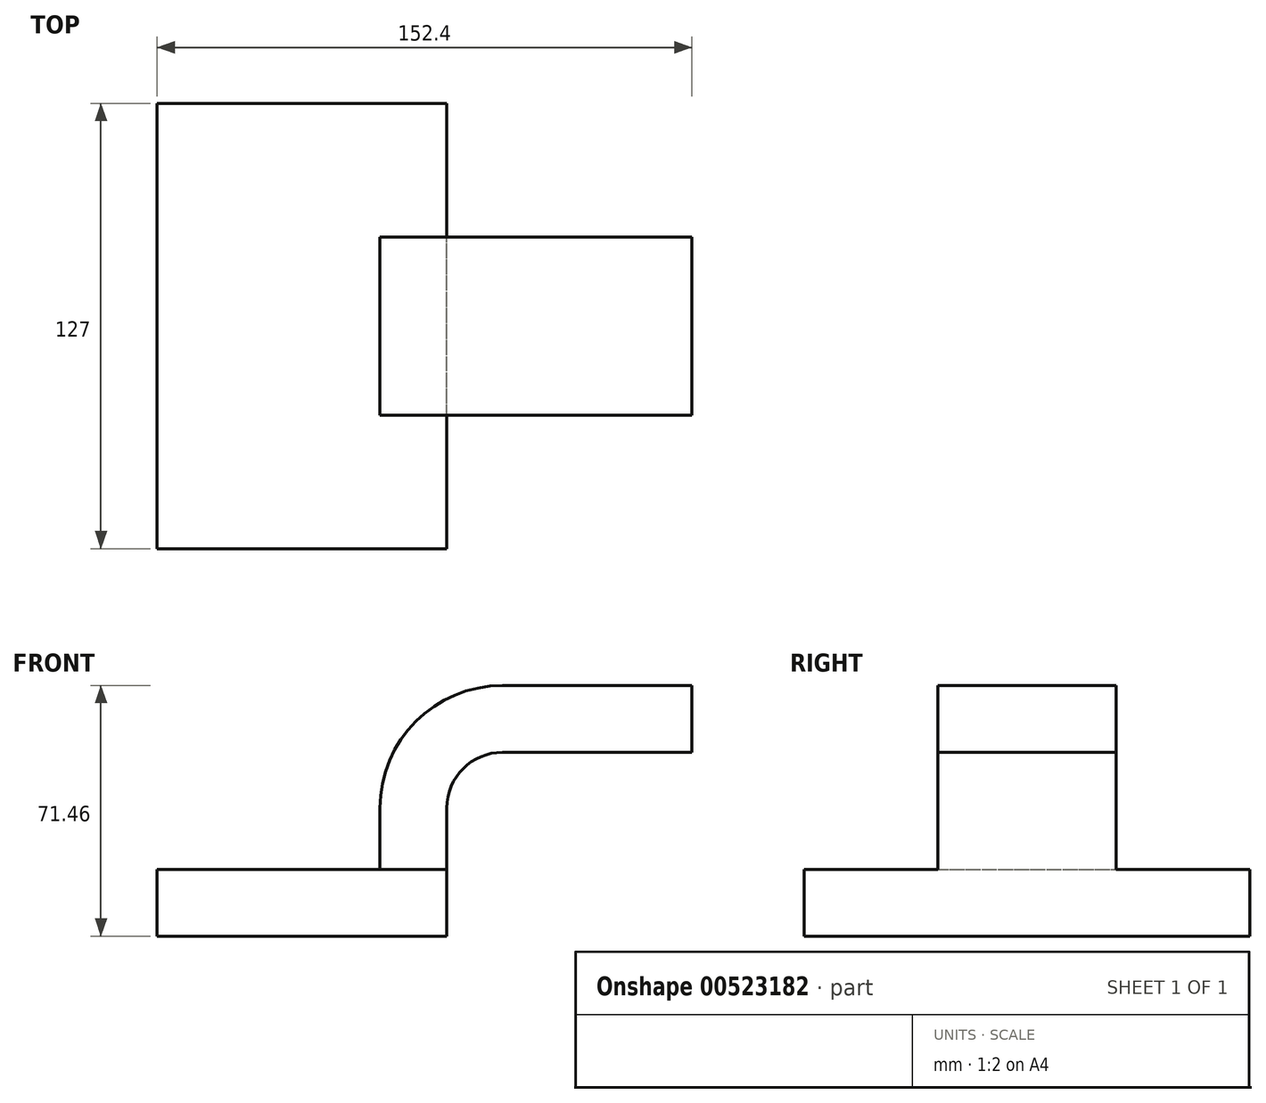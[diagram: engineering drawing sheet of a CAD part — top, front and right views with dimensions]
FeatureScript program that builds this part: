
annotation { "Feature Type Name" : "Feature", "Feature Type Description" : "" }
export const myFeature = defineFeature(function(context is Context, id is Id, definition is map)
    precondition{}
    {
        {
            var Q0;
            Q0=qCreatedBy(makeId("Front.planeOp"),FACE);
            var sketch = newSketch(context, id + "F0", { "sketchPlane" : qUnion([Q0])});
            skLineSegment(sketch, "E0.bottom", {"start": v(41.27, 9.53) * mm, "end": v(-41.28, 9.53) * mm});
            skLineSegment(sketch, "E0.top", {"start": v(41.28, -9.52) * mm, "end": v(-41.27, -9.52) * mm});
            skLineSegment(sketch, "E0.left", {"start": v(41.27, 9.53) * mm, "end": v(41.28, -9.52) * mm});
            skLineSegment(sketch, "E0.right", {"start": v(-41.28, 9.53) * mm, "end": v(-41.27, -9.52) * mm});
            skPoint(sketch, "E0.middle", {"position": v(0, 0) * mm});
            skLineSegment(sketch, "E1.bottom", {"start": v(60.32, 66.68) * mm, "end": v(111.12, 66.68) * mm});
            skLineSegment(sketch, "E1.top", {"start": v(60.32, 38.1) * mm, "end": v(111.12, 38.1) * mm});
            skLineSegment(sketch, "E1.left", {"start": v(60.32, 66.68) * mm, "end": v(60.32, 38.1) * mm});
            skLineSegment(sketch, "E1.right", {"start": v(111.12, 66.68) * mm, "end": v(111.12, 38.1) * mm});
            skPoint(sketch, "E1.middle", {"position": v(85.72, 52.39) * mm});
            skLineSegment(sketch, "E2", {"start": v(41.27, 9.53) * mm, "end": v(41.27, 27) * mm});
            skArc(sketch, "E3", {"start": v(41.27, 27) * mm, "mid": v(45.92, 38.23) * mm, "end": v(57.15, 42.88) * mm});
            skLineSegment(sketch, "E4", {"start": v(57.15, 42.88) * mm, "end": v(114.28, 42.88) * mm});
            skLineSegment(sketch, "E5.0", {"start": v(57.15, 61.93) * mm, "end": v(114.28, 61.93) * mm});
            skArc(sketch, "E5.1", {"start": v(22.22, 27) * mm, "mid": v(32.45, 51.7) * mm, "end": v(57.15, 61.93) * mm});
            skLineSegment(sketch, "E5.2", {"start": v(22.22, 9.53) * mm, "end": v(22.22, 27) * mm});
            skFitSpline(sketch, "E6", {"points": [v(-41.28, 9.52) * mm, v(57.15, 61.93) * mm], "startDerivative": vector(5.1, 161.67) * mm, "endDerivative": vector(113.06, -3.5) * mm});
            skSolve(sketch);
        }
        {
            var Q0;
            Q0=makeQuery(id+"F0.imprint","IMPRINT",FACE,{"disambiguationData":[TD([[makeQuery(id+"F0.imprint","IMPRINT",EDGE,{"derivedFrom":sQuery(id+"F0.wireOp",EDGE,"E0.top")}),-1.0]])]});
            extrude(context, id + "F1", {"entities" : qUnion([Q0]), "endBound" : BoundingType.SYMMETRIC, "depth" : 127 * mm, "offsetDistance" : 25.4 * mm});
        }
        {
            var Q0;
            {var subQ1=sQuery(id+"F0.wireOp",EDGE,"E2");Q0=makeQuery(id+"F0.imprint","IMPRINT",FACE,{"disambiguationData":[TD([[makeQuery(id+"F0.imprint","IMPRINT",EDGE,{"derivedFrom":subQ1}),1.0]])]});}
            var Q1;
            {var subQ0=sQuery(id+"F0.wireOp",EDGE,"E5.0");var subQ1=sQuery(id+"F0.wireOp",EDGE,"E1.left");var subQ2=makeQuery(id+"F0.imprint","INTERSECT",VERTEX,{"derivedFrom":[subQ1,subQ0]});Q1=makeQuery(id+"F0.imprint","IMPRINT",FACE,{"disambiguationData":[TD([[makeQuery(id+"F0.imprint","IMPRINT",EDGE,{"disambiguationData":[TD([[subQ2,-1.0]])],"derivedFrom":subQ1}),1.0]])]});}
            extrude(context, id + "F2", {"entities" : qUnion([Q0, Q1]), "operationType" : NewBodyOperationType.ADD, "endBound" : BoundingType.SYMMETRIC, "depth" : 50.8 * mm, "offsetDistance" : 25.4 * mm});
        }
        {
            var Q0;
            Q0=makeQuery(id+"F0.imprint","IMPRINT",FACE,{"disambiguationData":[TD([[makeQuery(id+"F0.imprint","IMPRINT",EDGE,{"derivedFrom":sQuery(id+"F0.wireOp",EDGE,"E5.1")}),1.0]])]});
            extrude(context, id + "F3", {"entities" : qUnion([Q0]), "operationType" : NewBodyOperationType.ADD, "endBound" : BoundingType.SYMMETRIC, "depth" : 15.88 * mm, "offsetDistance" : 25.4 * mm});
        }
    });
